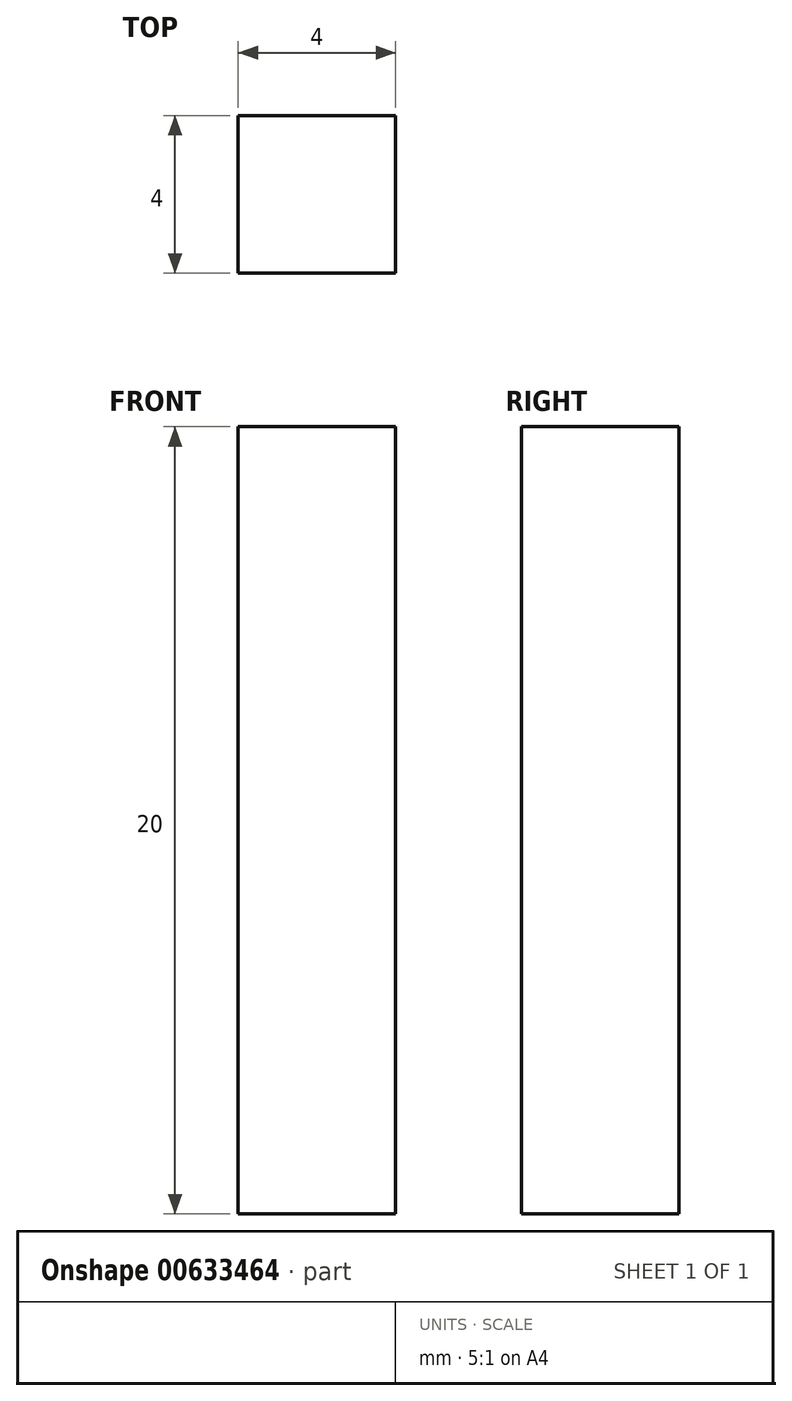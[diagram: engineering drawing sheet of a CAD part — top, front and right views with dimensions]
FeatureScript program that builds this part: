
annotation { "Feature Type Name" : "Feature", "Feature Type Description" : "" }
export const myFeature = defineFeature(function(context is Context, id is Id, definition is map)
    precondition{}
    {
        {
            var Q0;
            Q0=qCreatedBy(makeId("Right.planeOp"),FACE);
            var sketch = newSketch(context, id + "F0", { "sketchPlane" : qUnion([Q0])});
            skLineSegment(sketch, "E0.bottom", {"start": v(0, 0) * mm, "end": v(-300, 0) * mm});
            skLineSegment(sketch, "E0.left", {"start": v(0, 0) * mm, "end": v(0, 45) * mm});
            skLineSegment(sketch, "E0.right", {"start": v(-300, 0) * mm, "end": v(-300, 40) * mm});
            skLineSegment(sketch, "E1.right", {"start": v(-300, 40) * mm, "end": v(-300, 105) * mm});
            skLineSegment(sketch, "E2", {"start": v(-300, 105) * mm, "end": v(0, 45) * mm});
            skLineSegment(sketch, "E3.bottom", {"start": v(-240, 0) * mm, "end": v(-180, 0) * mm});
            skLineSegment(sketch, "E3.top", {"start": v(-240, 4) * mm, "end": v(-180, 4) * mm});
            skLineSegment(sketch, "E3.left", {"start": v(-240, 0) * mm, "end": v(-240, 4) * mm});
            skLineSegment(sketch, "E3.right", {"start": v(-180, 0) * mm, "end": v(-180, 4) * mm});
            skLineSegment(sketch, "E4.bottom", {"start": v(-120, 0) * mm, "end": v(-60, 0) * mm});
            skLineSegment(sketch, "E4.top", {"start": v(-120, 4) * mm, "end": v(-60, 4) * mm});
            skLineSegment(sketch, "E4.left", {"start": v(-120, 0) * mm, "end": v(-120, 4) * mm});
            skLineSegment(sketch, "E4.right", {"start": v(-60, 0) * mm, "end": v(-60, 4) * mm});
            skLineSegment(sketch, "E5.bottom", {"start": v(-300, 20) * mm, "end": v(-296, 20) * mm});
            skLineSegment(sketch, "E5.top", {"start": v(-300, 40) * mm, "end": v(-296, 40) * mm});
            skLineSegment(sketch, "E5.left", {"start": v(-300, 20) * mm, "end": v(-300, 40) * mm});
            skLineSegment(sketch, "E5.right", {"start": v(-296, 20) * mm, "end": v(-296, 40) * mm});
            skLineSegment(sketch, "E6.bottom", {"start": v(0, 40) * mm, "end": v(-4, 40) * mm});
            skLineSegment(sketch, "E6.top", {"start": v(0, 20) * mm, "end": v(-4, 20) * mm});
            skLineSegment(sketch, "E6.left", {"start": v(0, 40) * mm, "end": v(0, 20) * mm});
            skLineSegment(sketch, "E6.right", {"start": v(-4, 40) * mm, "end": v(-4, 20) * mm});
            skLineSegment(sketch, "E7.bottom", {"start": v(-250, 95) * mm, "end": v(-200.97, 85.2) * mm});
            skLineSegment(sketch, "E7.top", {"start": v(-250, 91) * mm, "end": v(-200.97, 81.2) * mm});
            skLineSegment(sketch, "E7.left", {"start": v(-250, 95) * mm, "end": v(-250, 91) * mm});
            skLineSegment(sketch, "E7.right", {"start": v(-200.97, 85.2) * mm, "end": v(-200.97, 81.2) * mm});
            skLineSegment(sketch, "E8.bottom", {"start": v(-150.97, 75.2) * mm, "end": v(-101.94, 65.39) * mm});
            skLineSegment(sketch, "E8.top", {"start": v(-150.97, 71.2) * mm, "end": v(-101.94, 61.39) * mm});
            skLineSegment(sketch, "E8.left", {"start": v(-150.97, 75.2) * mm, "end": v(-150.97, 71.2) * mm});
            skLineSegment(sketch, "E8.right", {"start": v(-101.94, 65.39) * mm, "end": v(-101.94, 61.39) * mm});
            skLineSegment(sketch, "E9.bottom", {"start": v(-68.2, 58.64) * mm, "end": v(-19.18, 48.84) * mm});
            skLineSegment(sketch, "E9.top", {"start": v(-68.2, 54.64) * mm, "end": v(-19.18, 44.84) * mm});
            skLineSegment(sketch, "E9.left", {"start": v(-68.2, 58.64) * mm, "end": v(-68.2, 54.64) * mm});
            skLineSegment(sketch, "E9.right", {"start": v(-19.18, 48.84) * mm, "end": v(-19.18, 44.84) * mm});
            skLineSegment(sketch, "E10", {"start": v(-19.18, 48.84) * mm, "end": v(0, 45) * mm});
            skSolve(sketch);
        }
        {
            var Q0;
            {var subQ13=sQuery(id+"F0.wireOp",EDGE,"E0.right");Q0=makeQuery(id+"F0.imprint","IMPRINT",FACE,{"disambiguationData":[TD([[makeQuery(id+"F0.imprint","IMPRINT",EDGE,{"derivedFrom":subQ13}),-1.0]])]});}
            extrude(context, id + "F1", {"entities" : qUnion([Q0]), "depth" : 4 * mm, "offsetDistance" : 25 * mm});
        }
    });
